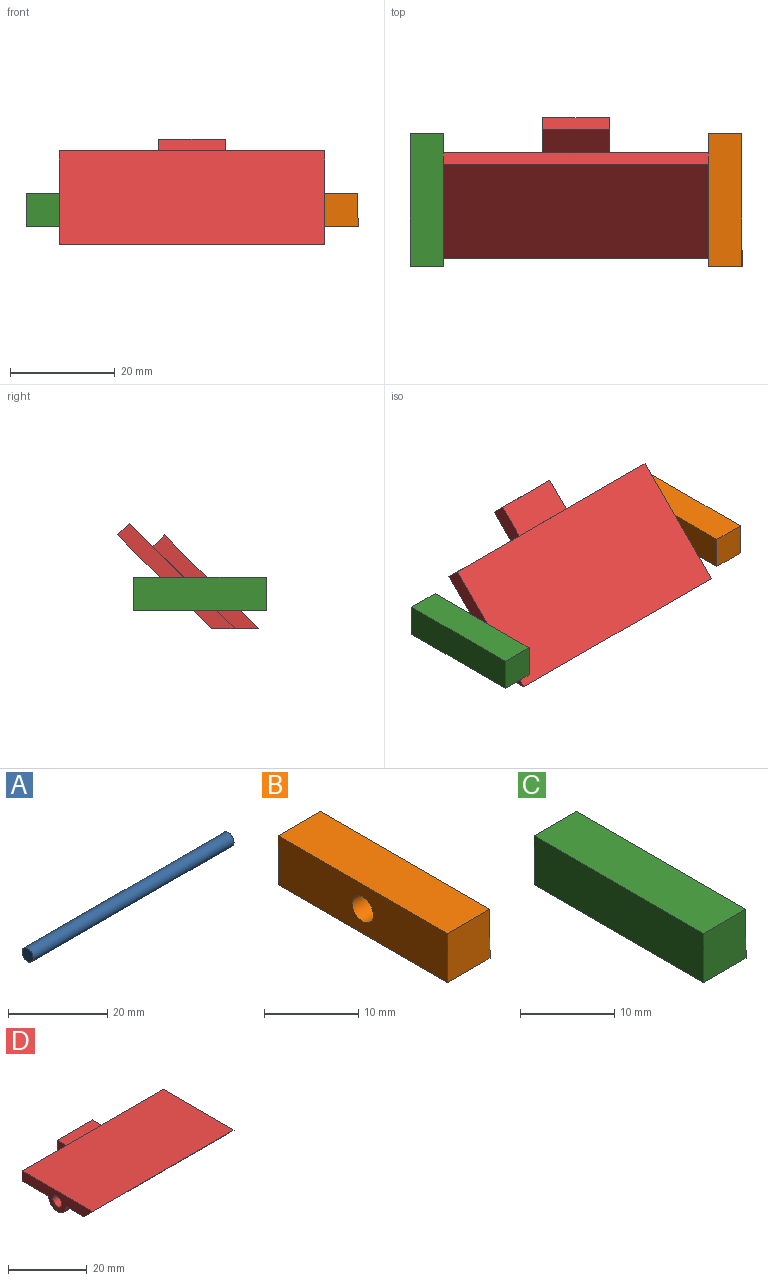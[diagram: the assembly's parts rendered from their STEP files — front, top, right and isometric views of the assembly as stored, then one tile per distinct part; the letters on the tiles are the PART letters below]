
ASSEMBLY  parts=4 mates=3
PART A: 3 faces, bbox 57.2x3.2x3.2 mm
  f0: cylinder r=1.59mm len=57.15mm, axis (-1,0,0), area 570mm2, adj f1,f2
  f1: plane 3.18x3.18mm, normal (1,0,0), area 7.9mm2, adj f0
  f2: plane 3.18x3.18mm, normal (-1,0,0), area 7.9mm2, adj f0
PART B: 12 faces, bbox 6.4x25.4x6.4 mm
  f0: cylinder r=1.59mm len=3.18mm, axis (0,0,1), area 31.7mm2, adj f5,f11
  f1: cylinder r=1.59mm len=3.18mm, axis (0,0,1), area 31.7mm2, adj f5,f10
  f2: cylinder r=1.59mm len=3.18mm, axis (1,0,0), area 31.7mm2, adj f8,f9
  f3: plane 25.4x6.35mm, normal (1,0,0), area 161.3mm2, adj f4,f5,f6,f7
  f4: plane 25.4x6.35mm, normal (0,0,1), area 161.3mm2, adj f3,f6,f7,f8
  f5: plane 25.4x6.35mm, normal (0,0,-1), area 145.5mm2, adj f0,f1,f3,f6,f7,f8
  f6: plane 6.35x6.35mm, normal (0,1,0), area 40.3mm2, adj f3,f4,f5,f8
  f7: plane 6.35x6.35mm, normal (0,-1,0), area 40.3mm2, adj f3,f4,f5,f8
  f8: plane 25.4x6.35mm, normal (-1,0,0), area 153.4mm2, adj f2,f4,f5,f6,f7
  f9: plane 3.18x3.18mm, normal (-1,0,0), area 7.9mm2, adj f2
  f10: plane 3.18x3.18mm, normal (0,0,-1), area 7.9mm2, adj f1
  f11: plane 3.18x3.18mm, normal (0,0,-1), area 7.9mm2, adj f0
PART C: 12 faces, bbox 6.4x25.4x6.4 mm
  f0: cylinder r=1.59mm len=3.18mm, axis (0,0,1), area 31.7mm2, adj f4,f11
  f1: cylinder r=1.59mm len=3.18mm, axis (0,0,1), area 31.7mm2, adj f4,f10
  f2: cylinder r=1.59mm len=3.18mm, axis (1,0,0), area 31.7mm2, adj f8,f9
  f3: plane 25.4x6.35mm, normal (0,0,1), area 161.3mm2, adj f5,f6,f7,f8
  f4: plane 25.4x6.35mm, normal (0,0,-1), area 145.5mm2, adj f0,f1,f5,f6,f7,f8
  f5: plane 25.4x6.35mm, normal (-1,0,0), area 161.3mm2, adj f3,f4,f6,f7
  f6: plane 6.35x6.35mm, normal (0,-1,0), area 40.3mm2, adj f3,f4,f5,f8
  f7: plane 6.35x6.35mm, normal (0,1,0), area 40.3mm2, adj f3,f4,f5,f8
  f8: plane 25.4x6.35mm, normal (1,0,0), area 153.4mm2, adj f2,f3,f4,f6,f7
  f9: plane 3.18x3.18mm, normal (1,0,0), area 7.9mm2, adj f2
  f10: plane 3.18x3.18mm, normal (0,0,-1), area 7.9mm2, adj f1
  f11: plane 3.18x3.18mm, normal (0,0,-1), area 7.9mm2, adj f0
PART D: 19 faces, bbox 50.8x31.8x6.4 mm
  f0: plane 50.8x3.18mm, normal (0,1,0), area 161.3mm2, adj f1,f3,f10,f15,f17,f18
  f1: plane 50.8x25.4mm, normal (0,0,1), area 1290.3mm2, adj f0,f4,f17,f18
  f2: plane 19.05x7.94mm, normal (0,0,-1), area 141.1mm2, adj f4,f5,f9,f11,f12,f18
  f3: plane 19.05x11.11mm, normal (0,0,-1), area 201.6mm2, adj f0,f5,f9,f11,f12,f18
  f4: plane 50.8x6.35mm, normal (0,-0.71,-0.71), area 285.1mm2, adj f1,f2,f6,f7,f8,f9,f17,f18
  f5: cylinder r=1.59mm len=50.8mm, axis (1,0,0), area 380mm2, adj f2,f3,f7,f8,f9,f10,f12,f14
  f6: plane 25.4x12.7mm, normal (0,0,-1), area 322.6mm2, adj f4,f7,f9,f16
  f7: plane 28.58x3.18mm, normal (-1,0,0), area 81.7mm2, adj f4,f5,f6,f8,f10,f15,f16
  f8: plane 19.05x7.94mm, normal (0,0,-1), area 141.1mm2, adj f4,f5,f7,f13,f14,f17
  f9: plane 28.58x3.18mm, normal (1,0,0), area 81.7mm2, adj f2,f3,f4,f5,f6,f15,f16
  f10: plane 19.05x11.11mm, normal (0,0,-1), area 201.6mm2, adj f0,f5,f7,f13,f14,f17
  f11: cylinder r=3.17mm len=6.35mm, axis (1,0,0), area 63.3mm2, adj f2,f3,f12,f18
  f12: plane 6.35x3.18mm, normal (-1,0,0), area 11.9mm2, adj f2,f3,f5,f11
  f13: cylinder r=3.17mm len=6.35mm, axis (-1,0,0), area 63.3mm2, adj f8,f10,f14,f17
  f14: plane 6.35x3.18mm, normal (1,0,0), area 11.9mm2, adj f5,f8,f10,f13
  f15: plane 12.7x6.35mm, normal (0,0,1), area 80.6mm2, adj f0,f7,f9,f16
  f16: plane 12.7x3.18mm, normal (0,1,0), area 40.3mm2, adj f6,f7,f9,f15
  f17: plane 25.4x6.35mm, normal (-1,0,0), area 83.5mm2, adj f0,f1,f4,f5,f8,f10,f13
  f18: plane 25.4x6.35mm, normal (1,0,0), area 83.5mm2, adj f0,f1,f2,f3,f4,f5,f11
PLACE A rot(axis=(-0.98,-0.21,-0.03),0deg) t=(3.17,16.11,15.34)mm
PLACE B rot(axis=(-0.02,-0.99,-0.15),0deg) t=(0,3.41,15.34)mm
PLACE C t=(0,3.41,15.34)mm
PLACE D rot(axis=(1,0,0),45deg) t=(0,7.13,6.36)mm
MATE revolute D.f5 <-> A.f0  axis (1,0,0) through (31.75,16.11,15.34)mm
MATE fastened B.f2 <-> A.f0  axis (-1,0,0) through (60.32,16.11,15.34)mm
MATE fastened C.f2 <-> A.f0  axis (1,0,0) through (3.17,16.11,15.34)mm
